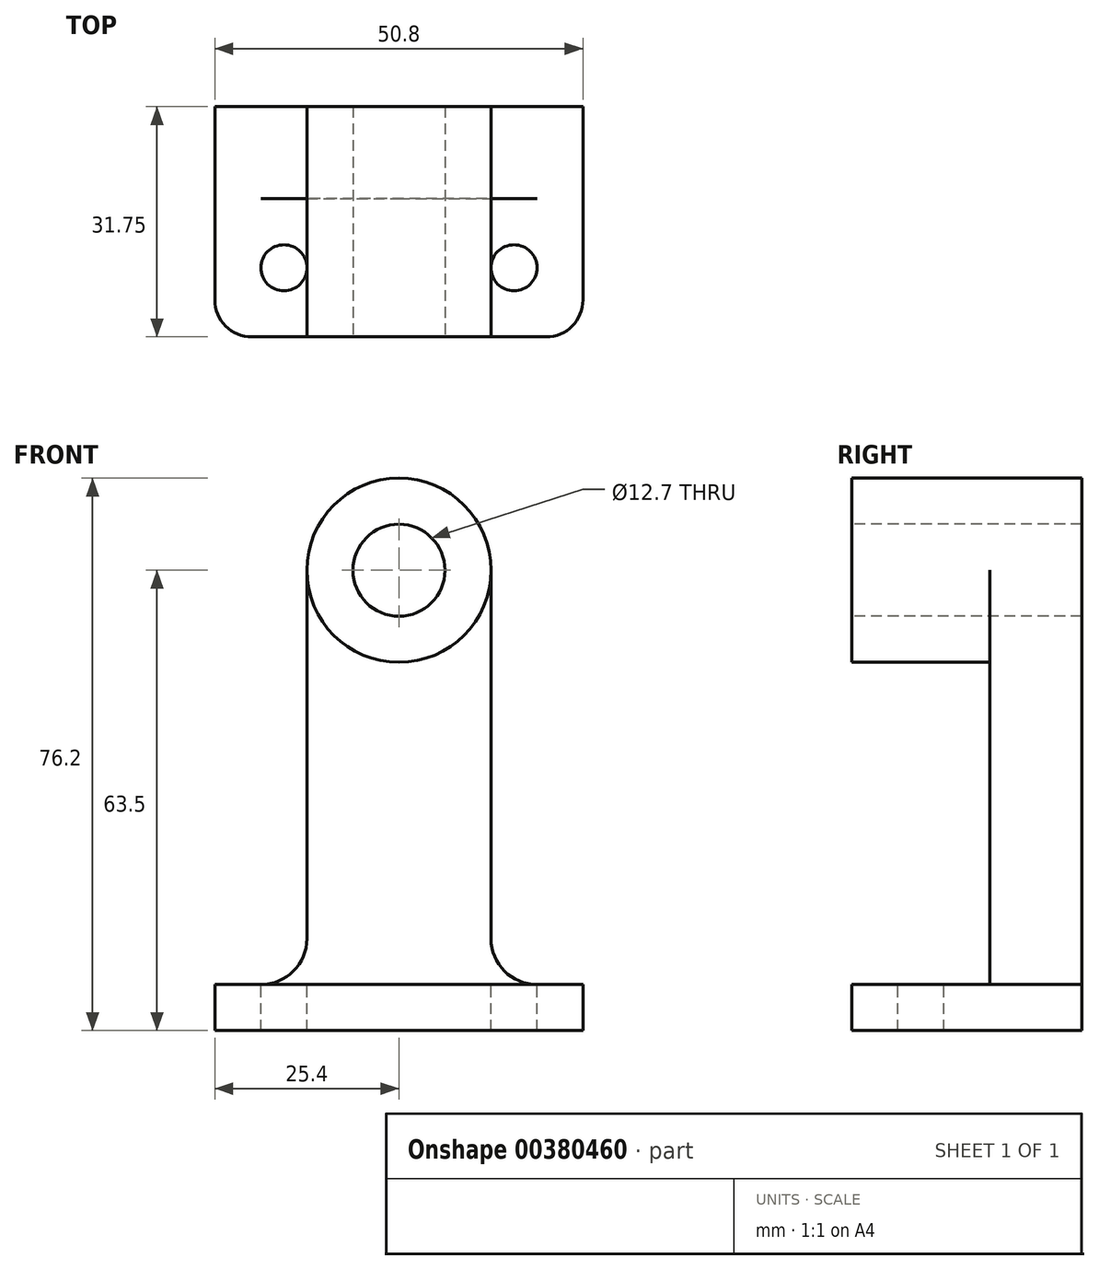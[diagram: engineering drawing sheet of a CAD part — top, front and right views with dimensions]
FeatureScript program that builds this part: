
annotation { "Feature Type Name" : "Feature", "Feature Type Description" : "" }
export const myFeature = defineFeature(function(context is Context, id is Id, definition is map)
    precondition{}
    {
        {
            var Q0;
            Q0=qCreatedBy(makeId("Top.planeOp"),FACE);
            var sketch = newSketch(context, id + "F0", { "sketchPlane" : qUnion([Q0])});
            skLineSegment(sketch, "E0", {"start": v(0, 0) * mm, "end": v(50.8, 0) * mm});
            skLineSegment(sketch, "E1", {"start": v(50.8, 0) * mm, "end": v(50.8, 31.75) * mm});
            skLineSegment(sketch, "E2", {"start": v(50.8, 31.75) * mm, "end": v(0, 31.75) * mm});
            skLineSegment(sketch, "E3", {"start": v(0, 31.75) * mm, "end": v(0, 0) * mm});
            skSolve(sketch);
        }
        {
            var Q0;
            Q0 = qSketchRegion(id + "F0", true);
            extrude(context, id + "F1", {"entities" : qUnion([Q0]), "depth" : 6.35 * mm, "offsetDistance" : 25.4 * mm});
        }
        {
            var Q0;
            Q0=makeQuery(id+"F1.opExtrude","CAP_FACE",FACE,{"disambiguationData":[OSD([sQuery(id+"F0.wireOp",EDGE,"E0"),sQuery(id+"F0.wireOp",EDGE,"E1"),sQuery(id+"F0.wireOp",EDGE,"E2"),sQuery(id+"F0.wireOp",EDGE,"E3")])],"isStart":false});
            var sketch = newSketch(context, id + "F2", { "sketchPlane" : qUnion([Q0])});
            skCircle(sketch, "E4", {"center": v(41.28, 9.53) * mm, "radius": 3.18 * mm});
            skCircle(sketch, "E5", {"center": v(9.53, 9.53) * mm, "radius": 3.18 * mm});
            skSolve(sketch);
        }
        {
            var Q0;
            Q0 = qSketchRegion(id + "F2", true);
            extrude(context, id + "F3", {"entities" : qUnion([Q0]), "operationType" : NewBodyOperationType.REMOVE, "oppositeDirection" : true, "depth" : 6.35 * mm, "offsetDistance" : 25.4 * mm});
        }
        {
            var Q0;
            Q0=makeQuery(id+"F1.opExtrude","SWEPT_FACE",FACE,{"disambiguationData":[OSD([sQuery(id+"F0.wireOp",EDGE,"E2")])]});
            var sketch = newSketch(context, id + "F4", { "sketchPlane" : qUnion([Q0])});
            skLineSegment(sketch, "E6", {"start": v(-38.1, 6.35) * mm, "end": v(-38.1, 76.2) * mm});
            skLineSegment(sketch, "E7", {"start": v(-38.1, 76.2) * mm, "end": v(-12.7, 76.2) * mm});
            skLineSegment(sketch, "E8", {"start": v(-12.7, 76.2) * mm, "end": v(-12.7, 6.35) * mm});
            skSolve(sketch);
        }
        {
            var Q0;
            Q0 = qSketchRegion(id + "F4", true);
            var Q1;
            {var subQ0=sQuery(id+"F4.wireOp",EDGE,"E6");Q1=makeQuery(id+"F4.imprint","IMPRINT",FACE,{"disambiguationData":[TD([[makeQuery(id+"F4.imprint","IMPRINT",EDGE,{"derivedFrom":subQ0}),-1.0]])]});}
            extrude(context, id + "F5", {"entities" : qUnion([Q0, Q1]), "operationType" : NewBodyOperationType.ADD, "oppositeDirection" : true, "depth" : 12.7 * mm, "offsetDistance" : 25.4 * mm});
        }
        {
            var Q0;
            Q0=makeQuery(id+"F5.opExtrude","CAP_FACE",FACE,{"disambiguationData":[OSD([sQuery(id+"F0.wireOp",EDGE,"E2"),sQuery(id+"F4.wireOp",EDGE,"E6"),sQuery(id+"F4.wireOp",EDGE,"E7"),sQuery(id+"F4.wireOp",EDGE,"E8")])],"isStart":false});
            var sketch = newSketch(context, id + "F6", { "sketchPlane" : qUnion([Q0])});
            skArc(sketch, "E9", {"start": v(38.1, 63.5) * mm, "mid": v(25.4, 76.2) * mm, "end": v(12.7, 63.5) * mm});
            skSolve(sketch);
        }
        {
            var Q0;
            Q0 = qSketchRegion(id + "F6", true);
            var Q1;
            {var subQ0=sQuery(id+"F6.wireOp",EDGE,"E9");var subQ1=makeQuery(id+"F5.opExtrude","CAP_EDGE",EDGE,{"disambiguationData":[OSD([sQuery(id+"F4.wireOp",EDGE,"E6")])],"isStart":false});var subQ2=makeQuery(id+"F6.imprint","INTERSECT",VERTEX,{"derivedFrom":[subQ1,subQ0]});Q1=makeQuery(id+"F6.imprint","IMPRINT",FACE,{"disambiguationData":[TD([[makeQuery(id+"F6.imprint","IMPRINT",EDGE,{"disambiguationData":[TD([[subQ2,-1.0]])],"derivedFrom":subQ0}),-1.0]])]});}
            var Q2;
            {var subQ0=sQuery(id+"F6.wireOp",EDGE,"E9");var subQ1=makeQuery(id+"F5.opExtrude","CAP_EDGE",EDGE,{"disambiguationData":[OSD([sQuery(id+"F4.wireOp",EDGE,"E8")])],"isStart":false});var subQ2=makeQuery(id+"F6.imprint","INTERSECT",VERTEX,{"derivedFrom":[subQ1,subQ0]});Q2=makeQuery(id+"F6.imprint","IMPRINT",FACE,{"disambiguationData":[TD([[makeQuery(id+"F6.imprint","IMPRINT",EDGE,{"disambiguationData":[TD([[subQ2,1.0]])],"derivedFrom":subQ0}),-1.0]])]});}
            extrude(context, id + "F7", {"entities" : qUnion([Q0, Q1, Q2]), "operationType" : NewBodyOperationType.REMOVE, "oppositeDirection" : true, "depth" : 25.4 * mm, "offsetDistance" : 25.4 * mm});
        }
        {
            var Q0;
            Q0=makeQuery(id+"F5.opExtrude","CAP_FACE",FACE,{"disambiguationData":[OSD([sQuery(id+"F0.wireOp",EDGE,"E2"),sQuery(id+"F4.wireOp",EDGE,"E6"),sQuery(id+"F4.wireOp",EDGE,"E7"),sQuery(id+"F4.wireOp",EDGE,"E8")])],"isStart":false});
            var sketch = newSketch(context, id + "F8", { "sketchPlane" : qUnion([Q0])});
            skCircle(sketch, "E10", {"center": v(25.4, 63.5) * mm, "radius": 12.7 * mm});
            skSolve(sketch);
        }
        {
            var Q0;
            Q0 = qSketchRegion(id + "F8", true);
            extrude(context, id + "F9", {"entities" : qUnion([Q0]), "operationType" : NewBodyOperationType.ADD, "depth" : 19.05 * mm, "offsetDistance" : 25.4 * mm});
        }
        {
            var Q0;
            Q0=makeQuery(id+"F9.opExtrude","CAP_FACE",FACE,{"disambiguationData":[OSD([sQuery(id+"F8.wireOp",EDGE,"E10")])],"isStart":false});
            var sketch = newSketch(context, id + "F10", { "sketchPlane" : qUnion([Q0])});
            skCircle(sketch, "E11", {"center": v(25.4, 63.5) * mm, "radius": 6.35 * mm});
            skSolve(sketch);
        }
        {
            var Q0;
            Q0 = qSketchRegion(id + "F10", true);
            extrude(context, id + "F11", {"entities" : qUnion([Q0]), "operationType" : NewBodyOperationType.REMOVE, "oppositeDirection" : true, "depth" : 31.75 * mm, "offsetDistance" : 25.4 * mm});
        }
        {
            var Q0;
            Q0=makeQuery(id+"F1.opExtrude","SWEPT_EDGE",EDGE,{"disambiguationData":[OSD([sQuery(id+"F0.wireOp",EDGE,"E0"),sQuery(id+"F0.wireOp",EDGE,"E3")])]});
            var Q1;
            Q1=makeQuery(id+"F1.opExtrude","SWEPT_EDGE",EDGE,{"disambiguationData":[OSD([sQuery(id+"F0.wireOp",EDGE,"E0"),sQuery(id+"F0.wireOp",EDGE,"E1")])]});
            fillet(context, id + "F12", {"entities" : qUnion([Q0, Q1]), "radius" : 5.08 * mm, "tangentPropagation" : true, "allowEdgeOverflow" : false});
        }
        {
            var Q0;
            Q0=makeQuery(id+"F5.opExtrude","SWEPT_FACE",FACE,{"disambiguationData":[OSD([sQuery(id+"F4.wireOp",EDGE,"E6")])]});
            var sketch = newSketch(context, id + "F13", { "sketchPlane" : qUnion([Q0])});
            skPoint(sketch, "E12.endSnap0", {"position": v(25.4, 6.35) * mm});
            skLineSegment(sketch, "E13", {"start": v(19.05, 19.05) * mm, "end": v(19.05, 6.35) * mm});
            skLineSegment(sketch, "E14", {"start": v(19.05, 19.05) * mm, "end": v(31.75, 19.05) * mm});
            skLineSegment(sketch, "E15", {"start": v(31.75, 19.05) * mm, "end": v(31.75, 6.35) * mm});
            skSolve(sketch);
        }
        {
            var Q0;
            Q0=makeQuery(id+"F13.imprint","IMPRINT",FACE,{"disambiguationData":[TD([[makeQuery(id+"F13.imprint","IMPRINT",EDGE,{"derivedFrom":sQuery(id+"F13.wireOp",EDGE,"E13")}),-1.0]])]});
            extrude(context, id + "F14", {"entities" : qUnion([Q0]), "operationType" : NewBodyOperationType.ADD, "depth" : 12.7 * mm, "offsetDistance" : 25.4 * mm});
        }
        {
            var Q0;
            Q0=makeQuery(id+"F14.boolean.opBoolean","MERGE",FACE,{"derivedFrom":[makeQuery(id+"F5.opExtrude","CAP_FACE",FACE,{"disambiguationData":[OSD([sQuery(id+"F0.wireOp",EDGE,"E2"),sQuery(id+"F4.wireOp",EDGE,"E6"),sQuery(id+"F4.wireOp",EDGE,"E7"),sQuery(id+"F4.wireOp",EDGE,"E8")])],"isStart":false}),makeQuery(id+"F14.opExtrude","SWEPT_FACE",FACE,{"disambiguationData":[OSD([sQuery(id+"F13.wireOp",EDGE,"E13")])]})]});
            var sketch = newSketch(context, id + "F15", { "sketchPlane" : qUnion([Q0])});
            skPoint(sketch, "E16.centerSnap0", {"position": v(50.8, 12.7) * mm});
            skLineSegment(sketch, "E17", {"start": v(38.1, 19.05) * mm, "end": v(38.1, 6.35) * mm});
            skCircle(sketch, "E18", {"center": v(44.45, 12.7) * mm, "radius": 6.35 * mm});
            skSolve(sketch);
        }
        {
            var Q0;
            Q0 = qSketchRegion(id + "F15", true);
            var Q1;
            {var subQ0=sQuery(id+"F15.wireOp",EDGE,"E18");var subQ1=sQuery(id+"F13.wireOp",EDGE,"E13");var subQ4=makeQuery(id+"F14.opExtrude","CAP_EDGE",EDGE,{"disambiguationData":[OSD([subQ1])],"isStart":false});var subQ5=makeQuery(id+"F15.imprint","INTERSECT",VERTEX,{"derivedFrom":[subQ4,subQ0]});Q1=makeQuery(id+"F15.imprint","IMPRINT",FACE,{"disambiguationData":[TD([[makeQuery(id+"F15.imprint","IMPRINT",EDGE,{"disambiguationData":[TD([[subQ5,-1.0]])],"derivedFrom":subQ0}),-1.0]])]});}
            var Q2;
            {var subQ0=sQuery(id+"F15.wireOp",EDGE,"E17");var subQ4=sQuery(id+"F15.wireOp",EDGE,"E18");var subQ5=makeQuery(id+"F15.imprint","INTERSECT",VERTEX,{"derivedFrom":[subQ0,subQ4]});Q2=makeQuery(id+"F15.imprint","IMPRINT",FACE,{"disambiguationData":[TD([[makeQuery(id+"F15.imprint","IMPRINT",EDGE,{"disambiguationData":[TD([[subQ5,1.0]])],"derivedFrom":subQ4}),-1.0]])]});}
            var Q3;
            {var subQ0=sQuery(id+"F15.wireOp",EDGE,"E18");var subQ1=sQuery(id+"F13.wireOp",EDGE,"E13");var subQ2=makeQuery(id+"F14.opExtrude","CAP_EDGE",EDGE,{"disambiguationData":[OSD([subQ1])],"isStart":false});var subQ3=makeQuery(id+"F15.imprint","INTERSECT",VERTEX,{"derivedFrom":[subQ2,subQ0]});Q3=makeQuery(id+"F15.imprint","IMPRINT",FACE,{"disambiguationData":[TD([[makeQuery(id+"F15.imprint","IMPRINT",EDGE,{"disambiguationData":[TD([[subQ3,1.0]])],"derivedFrom":subQ0}),-1.0]])]});}
            extrude(context, id + "F16", {"entities" : qUnion([Q0, Q1, Q2, Q3]), "operationType" : NewBodyOperationType.REMOVE, "oppositeDirection" : true, "depth" : 25.4 * mm, "offsetDistance" : 25.4 * mm});
        }
        {
            var Q0;
            Q0=makeQuery(id+"F5.opExtrude","SWEPT_FACE",FACE,{"disambiguationData":[OSD([sQuery(id+"F4.wireOp",EDGE,"E8")])]});
            var sketch = newSketch(context, id + "F17", { "sketchPlane" : qUnion([Q0])});
            skLineSegment(sketch, "E19", {"start": v(-31.75, 19.05) * mm, "end": v(-31.75, 6.35) * mm});
            skLineSegment(sketch, "E20", {"start": v(-31.75, 19.05) * mm, "end": v(-19.05, 19.05) * mm});
            skLineSegment(sketch, "E21", {"start": v(-19.05, 19.05) * mm, "end": v(-19.05, 6.35) * mm});
            skSolve(sketch);
        }
        {
            var Q0;
            Q0 = qSketchRegion(id + "F17", true);
            var Q1;
            Q1=makeQuery(id+"F17.imprint","IMPRINT",FACE,{"disambiguationData":[TD([[makeQuery(id+"F17.imprint","IMPRINT",EDGE,{"derivedFrom":sQuery(id+"F17.wireOp",EDGE,"E19")}),1.0]])]});
            extrude(context, id + "F18", {"entities" : qUnion([Q0, Q1]), "operationType" : NewBodyOperationType.ADD, "depth" : 12.7 * mm, "offsetDistance" : 25.4 * mm});
        }
        {
            var Q0;
            Q0=makeQuery(id+"F18.boolean.opBoolean","MERGE",FACE,{"derivedFrom":[makeQuery(id+"F14.boolean.opBoolean","MERGE",FACE,{"derivedFrom":[makeQuery(id+"F5.opExtrude","CAP_FACE",FACE,{"disambiguationData":[OSD([sQuery(id+"F0.wireOp",EDGE,"E2"),sQuery(id+"F4.wireOp",EDGE,"E6"),sQuery(id+"F4.wireOp",EDGE,"E7"),sQuery(id+"F4.wireOp",EDGE,"E8")])],"isStart":false}),makeQuery(id+"F14.opExtrude","SWEPT_FACE",FACE,{"disambiguationData":[OSD([sQuery(id+"F13.wireOp",EDGE,"E13")])]})]}),makeQuery(id+"F18.opExtrude","SWEPT_FACE",FACE,{"disambiguationData":[OSD([sQuery(id+"F17.wireOp",EDGE,"E21")])]})]});
            var sketch = newSketch(context, id + "F19", { "sketchPlane" : qUnion([Q0])});
            skLineSegment(sketch, "E22", {"start": v(12.7, 19.05) * mm, "end": v(12.7, 6.35) * mm});
            skCircle(sketch, "E23", {"center": v(6.35, 12.7) * mm, "radius": 6.35 * mm});
            skPoint(sketch, "E23.centerSnap0", {"position": v(0, 12.7) * mm});
            skSolve(sketch);
        }
        {
            var Q0;
            {var subQ0=sQuery(id+"F19.wireOp",EDGE,"E23");var subQ1=makeQuery(id+"F19.imprint","INTERSECT",VERTEX,{"derivedFrom":[sQuery(id+"F19.wireOp",EDGE,"E22"),subQ0]});Q0=makeQuery(id+"F19.imprint","IMPRINT",FACE,{"disambiguationData":[TD([[makeQuery(id+"F19.imprint","IMPRINT",EDGE,{"disambiguationData":[TD([[subQ1,-1.0]])],"derivedFrom":subQ0}),1.0]])]});}
            var Q1;
            {var subQ0=sQuery(id+"F19.wireOp",EDGE,"E23");var subQ1=sQuery(id+"F17.wireOp",EDGE,"E21");var subQ4=makeQuery(id+"F18.opExtrude","CAP_EDGE",EDGE,{"disambiguationData":[OSD([subQ1])],"isStart":false});var subQ5=makeQuery(id+"F19.imprint","INTERSECT",VERTEX,{"derivedFrom":[subQ4,subQ0]});Q1=makeQuery(id+"F19.imprint","IMPRINT",FACE,{"disambiguationData":[TD([[makeQuery(id+"F19.imprint","IMPRINT",EDGE,{"disambiguationData":[TD([[subQ5,1.0]])],"derivedFrom":subQ0}),-1.0]])]});}
            var Q2;
            {var subQ0=sQuery(id+"F19.wireOp",EDGE,"E23");var subQ1=sQuery(id+"F17.wireOp",EDGE,"E21");var subQ2=makeQuery(id+"F18.opExtrude","CAP_EDGE",EDGE,{"disambiguationData":[OSD([subQ1])],"isStart":false});var subQ3=makeQuery(id+"F19.imprint","INTERSECT",VERTEX,{"derivedFrom":[subQ2,subQ0]});Q2=makeQuery(id+"F19.imprint","IMPRINT",FACE,{"disambiguationData":[TD([[makeQuery(id+"F19.imprint","IMPRINT",EDGE,{"disambiguationData":[TD([[subQ3,-1.0]])],"derivedFrom":subQ0}),-1.0]])]});}
            var Q3;
            {var subQ0=sQuery(id+"F19.wireOp",EDGE,"E22");var subQ4=sQuery(id+"F19.wireOp",EDGE,"E23");var subQ5=makeQuery(id+"F19.imprint","INTERSECT",VERTEX,{"derivedFrom":[subQ0,subQ4]});Q3=makeQuery(id+"F19.imprint","IMPRINT",FACE,{"disambiguationData":[TD([[makeQuery(id+"F19.imprint","IMPRINT",EDGE,{"disambiguationData":[TD([[subQ5,-1.0]])],"derivedFrom":subQ4}),-1.0]])]});}
            extrude(context, id + "F20", {"entities" : qUnion([Q0, Q1, Q2, Q3]), "operationType" : NewBodyOperationType.REMOVE, "oppositeDirection" : true, "depth" : 25.4 * mm});
        }
    });
